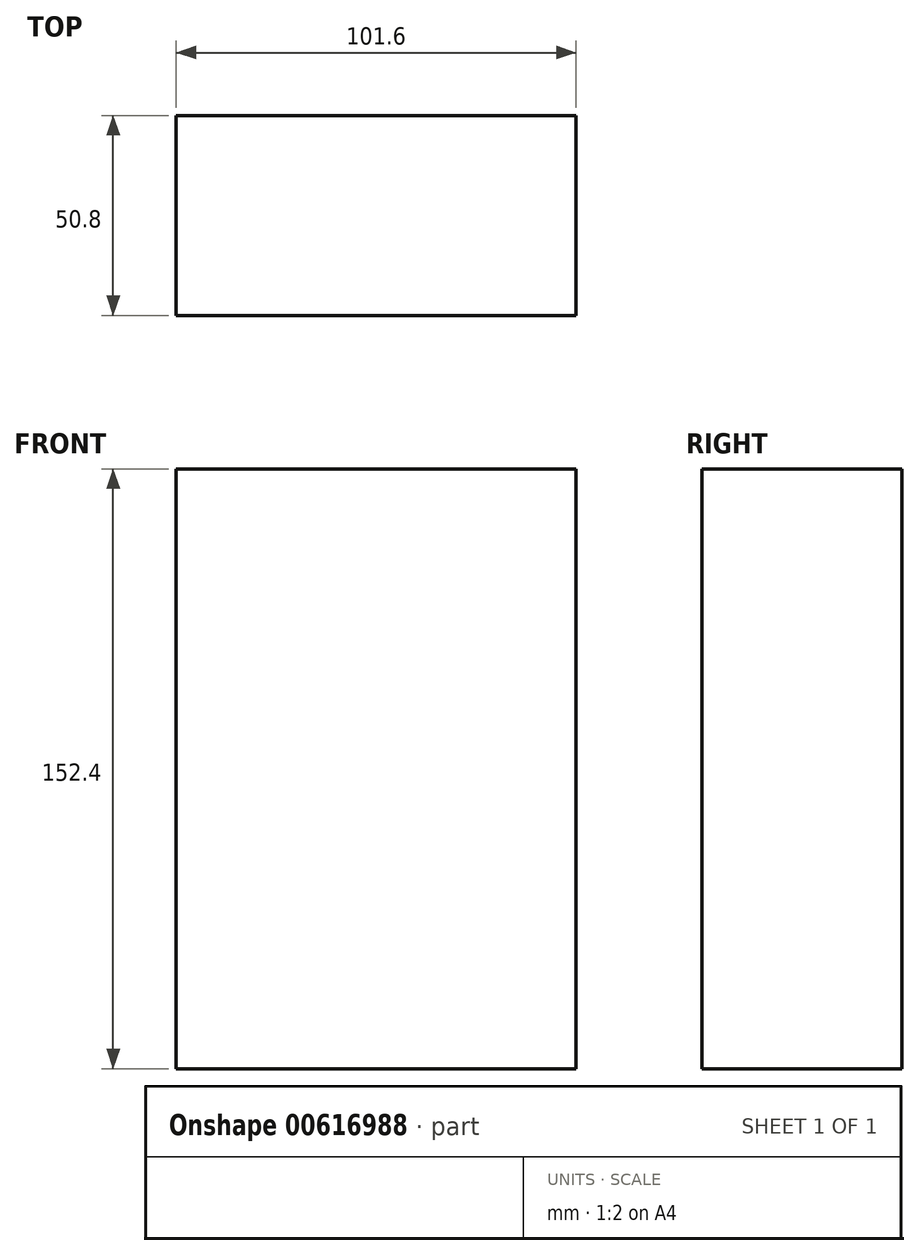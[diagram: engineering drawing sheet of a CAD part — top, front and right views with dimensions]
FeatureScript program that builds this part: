
annotation { "Feature Type Name" : "Feature", "Feature Type Description" : "" }
export const myFeature = defineFeature(function(context is Context, id is Id, definition is map)
    precondition{}
    {
        {
            var Q0;
            Q0=qCreatedBy(makeId("Front.planeOp"),FACE);
            var sketch = newSketch(context, id + "F0", { "sketchPlane" : qUnion([Q0])});
            skPoint(sketch, "E0.middle", {"position": v(0, 0) * mm});
            skLineSegment(sketch, "E1", {"start": v(-56.12, 51.35) * mm, "end": v(56.12, 51.35) * mm});
            skPoint(sketch, "E2.endSnap0", {"position": v(0, -34.02) * mm});
            skLineSegment(sketch, "E3", {"start": v(-56.12, 0) * mm, "end": v(56.12, 0) * mm});
            skLineSegment(sketch, "E4", {"start": v(-56.12, -47.22) * mm, "end": v(45.48, -47.22) * mm});
            skLineSegment(sketch, "E5", {"start": v(-56.12, 105.18) * mm, "end": v(45.48, 105.18) * mm});
            skLineSegment(sketch, "E6", {"start": v(-56.12, 105.18) * mm, "end": v(-56.12, -47.22) * mm});
            skLineSegment(sketch, "E7", {"start": v(45.48, -47.22) * mm, "end": v(45.48, 105.18) * mm});
            skLineSegment(sketch, "E8", {"start": v(-5.32, 105.18) * mm, "end": v(-5.32, -47.22) * mm});
            skSolve(sketch);
        }
        {
            var Q0;
            Q0=qCreatedBy(makeId("Front.planeOp"),FACE);
            var sketch = newSketch(context, id + "F1", { "sketchPlane" : qUnion([Q0])});
            skSolve(sketch);
        }
        {
            var Q0;
            Q0 = qSketchRegion(id + "F1", true);
            var Q1;
            {var subQ0=sQuery(id+"F0.wireOp",EDGE,"E6");var subQ1=sQuery(id+"F0.wireOp",EDGE,"E1");var subQ2=makeQuery(id+"F0.imprint","INTERSECT",VERTEX,{"derivedFrom":[subQ1,subQ0]});Q1=makeQuery(id+"F0.imprint","IMPRINT",FACE,{"disambiguationData":[TD([[makeQuery(id+"F0.imprint","IMPRINT",EDGE,{"disambiguationData":[TD([[subQ2,-1.0]])],"derivedFrom":subQ1}),1.0]])]});}
            var Q2;
            {var subQ0=sQuery(id+"F0.wireOp",EDGE,"E7");var subQ1=sQuery(id+"F0.wireOp",EDGE,"E1");var subQ2=makeQuery(id+"F0.imprint","INTERSECT",VERTEX,{"derivedFrom":[subQ1,subQ0]});Q2=makeQuery(id+"F0.imprint","IMPRINT",FACE,{"disambiguationData":[TD([[makeQuery(id+"F0.imprint","IMPRINT",EDGE,{"disambiguationData":[TD([[subQ2,1.0]])],"derivedFrom":subQ1}),1.0]])]});}
            var Q3;
            {var subQ0=sQuery(id+"F0.wireOp",EDGE,"E6");var subQ1=sQuery(id+"F0.wireOp",EDGE,"E1");var subQ2=makeQuery(id+"F0.imprint","INTERSECT",VERTEX,{"derivedFrom":[subQ1,subQ0]});Q3=makeQuery(id+"F0.imprint","IMPRINT",FACE,{"disambiguationData":[TD([[makeQuery(id+"F0.imprint","IMPRINT",EDGE,{"disambiguationData":[TD([[subQ2,-1.0]])],"derivedFrom":subQ1}),-1.0]])]});}
            var Q4;
            {var subQ0=sQuery(id+"F0.wireOp",EDGE,"E7");var subQ1=sQuery(id+"F0.wireOp",EDGE,"E1");var subQ2=makeQuery(id+"F0.imprint","INTERSECT",VERTEX,{"derivedFrom":[subQ1,subQ0]});Q4=makeQuery(id+"F0.imprint","IMPRINT",FACE,{"disambiguationData":[TD([[makeQuery(id+"F0.imprint","IMPRINT",EDGE,{"disambiguationData":[TD([[subQ2,1.0]])],"derivedFrom":subQ1}),-1.0]])]});}
            var Q5;
            {var subQ0=sQuery(id+"F0.wireOp",EDGE,"E6");var subQ1=sQuery(id+"F0.wireOp",EDGE,"E3");var subQ2=makeQuery(id+"F0.imprint","INTERSECT",VERTEX,{"derivedFrom":[subQ1,subQ0]});Q5=makeQuery(id+"F0.imprint","IMPRINT",FACE,{"disambiguationData":[TD([[makeQuery(id+"F0.imprint","IMPRINT",EDGE,{"disambiguationData":[TD([[subQ2,-1.0]])],"derivedFrom":subQ1}),-1.0]])]});}
            var Q6;
            {var subQ0=sQuery(id+"F0.wireOp",EDGE,"E7");var subQ1=sQuery(id+"F0.wireOp",EDGE,"E3");var subQ2=makeQuery(id+"F0.imprint","INTERSECT",VERTEX,{"derivedFrom":[subQ1,subQ0]});Q6=makeQuery(id+"F0.imprint","IMPRINT",FACE,{"disambiguationData":[TD([[makeQuery(id+"F0.imprint","IMPRINT",EDGE,{"disambiguationData":[TD([[subQ2,1.0]])],"derivedFrom":subQ1}),-1.0]])]});}
            extrude(context, id + "F2", {"entities" : qUnion([Q0, Q1, Q2, Q3, Q4, Q5, Q6]), "endBound" : BoundingType.SYMMETRIC, "depth" : 50.8 * mm, "offsetDistance" : 25.4 * mm});
        }
    });
